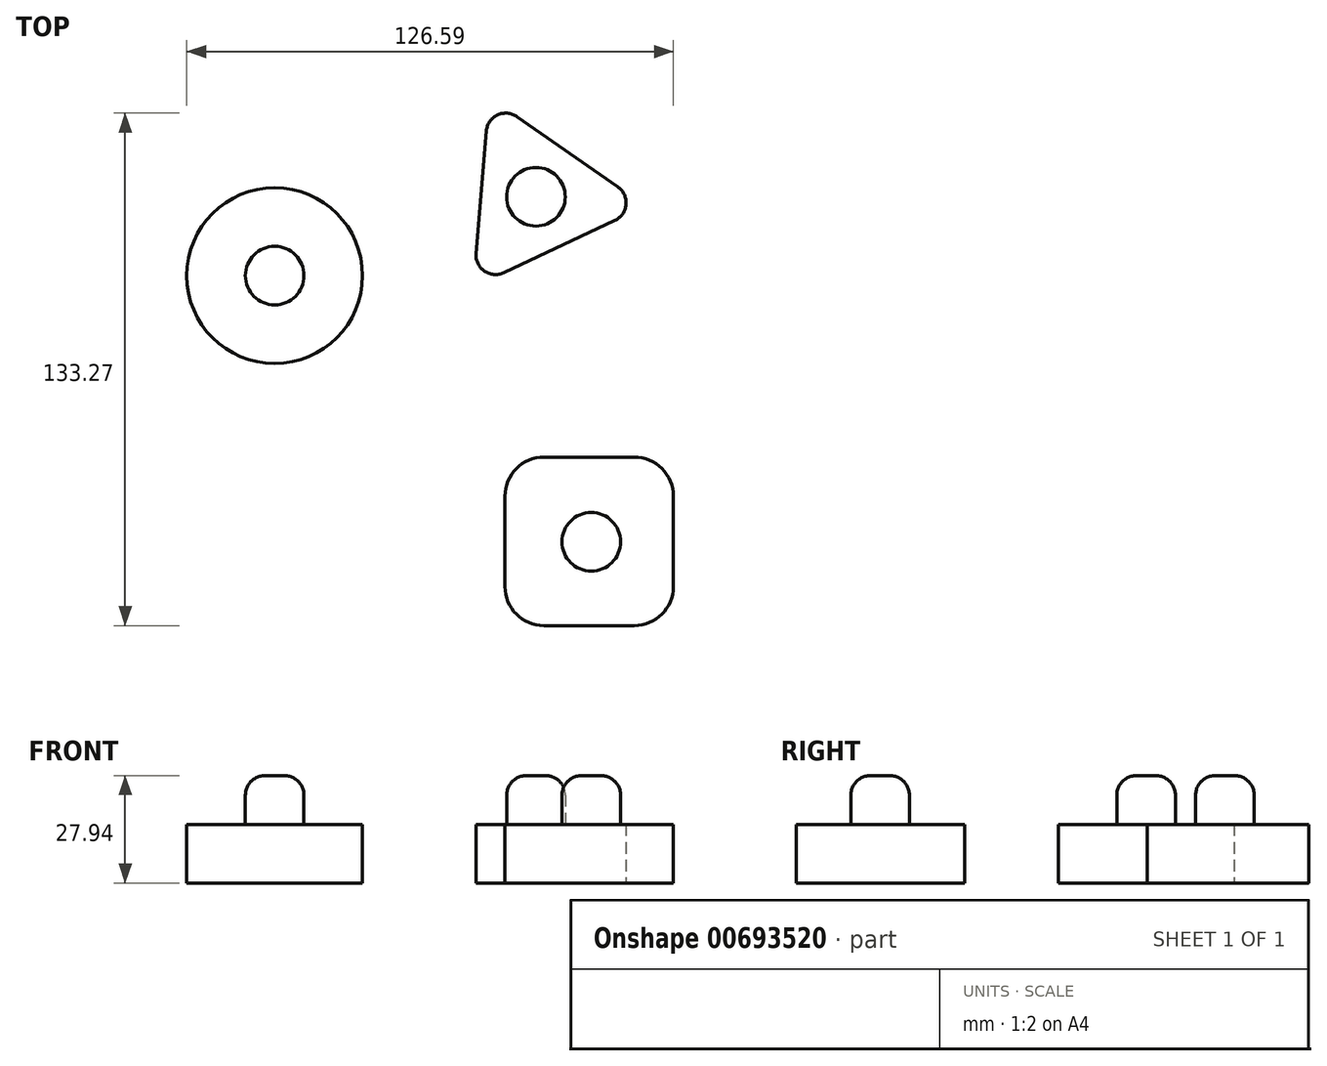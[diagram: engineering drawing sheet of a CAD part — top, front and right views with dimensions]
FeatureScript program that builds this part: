
annotation { "Feature Type Name" : "Feature", "Feature Type Description" : "" }
export const myFeature = defineFeature(function(context is Context, id is Id, definition is map)
    precondition{}
    {
        {
            var Q0;
            Q0=qCreatedBy(makeId("Top.planeOp"),FACE);
            var sketch = newSketch(context, id + "F0", { "sketchPlane" : qUnion([Q0])});
            skCircle(sketch, "E0", {"center": v(-45.19, 36.23) * mm, "radius": 22.86 * mm});
            skCircle(sketch, "E1", {"center": v(-45.19, 36.23) * mm, "radius": 7.62 * mm});
            skSolve(sketch);
        }
        {
            var Q0;
            Q0 = qSketchRegion(id + "F0", true);
            extrude(context, id + "F1", {"entities" : qUnion([Q0]), "depth" : 15.24 * mm, "offsetDistance" : 25.4 * mm});
        }
        {
            var Q0;
            Q0=qCreatedBy(makeId("Top.planeOp"),FACE);
            var sketch = newSketch(context, id + "F2", { "sketchPlane" : qUnion([Q0])});
            skLineSegment(sketch, "E2.bottom", {"start": v(24.88, -10.96) * mm, "end": v(48.38, -10.96) * mm});
            skLineSegment(sketch, "E2.top", {"start": v(24.88, -54.77) * mm, "end": v(48.38, -54.77) * mm});
            skLineSegment(sketch, "E2.left", {"start": v(14.72, -21.12) * mm, "end": v(14.72, -44.61) * mm});
            skLineSegment(sketch, "E2.right", {"start": v(58.54, -21.12) * mm, "end": v(58.54, -44.61) * mm});
            skPoint(sketch, "E3.visualSharp", {"position": v(14.72, -10.96) * mm});
            skArc(sketch, "E3.filletArc", {"start": v(24.88, -10.96) * mm, "mid": v(17.7, -13.93) * mm, "end": v(14.72, -21.12) * mm});
            skPoint(sketch, "E4.visualSharp", {"position": v(14.72, -54.77) * mm});
            skArc(sketch, "E4.filletArc", {"start": v(14.72, -44.61) * mm, "mid": v(17.7, -51.8) * mm, "end": v(24.88, -54.77) * mm});
            skPoint(sketch, "E5.visualSharp", {"position": v(58.54, -54.77) * mm});
            skArc(sketch, "E5.filletArc", {"start": v(48.38, -54.77) * mm, "mid": v(55.56, -51.8) * mm, "end": v(58.54, -44.61) * mm});
            skPoint(sketch, "E6.visualSharp", {"position": v(58.54, -10.96) * mm});
            skArc(sketch, "E7.filletArc", {"start": v(58.54, -21.12) * mm, "mid": v(55.56, -13.93) * mm, "end": v(48.38, -10.96) * mm});
            skCircle(sketch, "E8", {"center": v(37.19, -32.98) * mm, "radius": 7.62 * mm});
            skSolve(sketch);
        }
        {
            var Q0;
            Q0=makeQuery(id+"F2.imprint","IMPRINT",FACE,{"disambiguationData":[TD([[makeQuery(id+"F2.imprint","IMPRINT",EDGE,{"derivedFrom":sQuery(id+"F2.wireOp",EDGE,"E2.bottom")}),-1.0]])]});
            extrude(context, id + "F3", {"entities" : qUnion([Q0]), "depth" : 15.24 * mm, "offsetDistance" : 25.4 * mm});
        }
        {
            var Q0;
            Q0=qCreatedBy(makeId("Top.planeOp"),FACE);
            var sketch = newSketch(context, id + "F4", { "sketchPlane" : qUnion([Q0])});
            skCircle(sketch, "E9.cCircle", {"center": v(22.8, 56.73) * mm, "radius": 14.3 * mm, "construction": true});
            skLineSegment(sketch, "E9.0", {"start": v(43.33, 50.58) * mm, "end": v(14.43, 37) * mm});
            skLineSegment(sketch, "E9.1", {"start": v(7.2, 42.02) * mm, "end": v(9.9, 73.84) * mm});
            skLineSegment(sketch, "E9.2", {"start": v(17.86, 77.59) * mm, "end": v(44.07, 59.35) * mm});
            skPoint(sketch, "E9.0.midPoint", {"position": v(28.88, 43.8) * mm});
            skPoint(sketch, "E10.visualSharp", {"position": v(10.64, 82.61) * mm});
            skArc(sketch, "E10.filletArc", {"start": v(17.86, 77.59) * mm, "mid": v(12.8, 78.01) * mm, "end": v(9.9, 73.84) * mm});
            skPoint(sketch, "E11.visualSharp", {"position": v(51.3, 54.33) * mm});
            skArc(sketch, "E11.filletArc", {"start": v(43.33, 50.58) * mm, "mid": v(46.23, 54.75) * mm, "end": v(44.07, 59.35) * mm});
            skPoint(sketch, "E12.visualSharp", {"position": v(6.47, 33.26) * mm});
            skArc(sketch, "E12.filletArc", {"start": v(7.2, 42.02) * mm, "mid": v(9.37, 37.43) * mm, "end": v(14.43, 37) * mm});
            skCircle(sketch, "E13", {"center": v(22.8, 56.73) * mm, "radius": 7.62 * mm});
            skSolve(sketch);
        }
        {
            var Q0;
            Q0 = qSketchRegion(id + "F4", true);
            extrude(context, id + "F5", {"entities" : qUnion([Q0]), "depth" : 15.24 * mm, "offsetDistance" : 25.4 * mm});
        }
        {
            var Q0;
            Q0=makeQuery(id+"F2.imprint","IMPRINT",FACE,{"disambiguationData":[TD([[makeQuery(id+"F2.imprint","IMPRINT",EDGE,{"derivedFrom":sQuery(id+"F2.wireOp",EDGE,"E8")}),1.0]])]});
            extrude(context, id + "F6", {"entities" : qUnion([Q0]), "operationType" : NewBodyOperationType.ADD, "depth" : 27.94 * mm, "offsetDistance" : 25.4 * mm});
        }
        {
            var Q0;
            Q0=makeQuery(id+"F6.opExtrude","CAP_EDGE",EDGE,{"disambiguationData":[OSD([sQuery(id+"F2.wireOp",EDGE,"E8")])],"isStart":false});
            fillet(context, id + "F7", {"entities" : qUnion([Q0]), "radius" : 5.08 * mm, "tangentPropagation" : true, "allowEdgeOverflow" : false});
        }
        {
            var Q0;
            Q0=makeQuery(id+"F0.imprint","IMPRINT",FACE,{"disambiguationData":[TD([[makeQuery(id+"F0.imprint","IMPRINT",EDGE,{"derivedFrom":sQuery(id+"F0.wireOp",EDGE,"E1")}),1.0]])]});
            extrude(context, id + "F8", {"entities" : qUnion([Q0]), "operationType" : NewBodyOperationType.ADD, "depth" : 27.94 * mm, "offsetDistance" : 25.4 * mm});
        }
        {
            var Q0;
            Q0=makeQuery(id+"F8.opExtrude","CAP_EDGE",EDGE,{"disambiguationData":[OSD([sQuery(id+"F0.wireOp",EDGE,"E1")])],"isStart":false});
            fillet(context, id + "F9", {"entities" : qUnion([Q0]), "radius" : 5.08 * mm, "tangentPropagation" : true, "allowEdgeOverflow" : false});
        }
        {
            var Q0;
            Q0=makeQuery(id+"F4.imprint","IMPRINT",FACE,{"disambiguationData":[TD([[makeQuery(id+"F4.imprint","IMPRINT",EDGE,{"derivedFrom":sQuery(id+"F4.wireOp",EDGE,"E13")}),1.0]])]});
            extrude(context, id + "F10", {"entities" : qUnion([Q0]), "operationType" : NewBodyOperationType.ADD, "depth" : 27.94 * mm, "offsetDistance" : 25.4 * mm});
        }
        {
            var Q0;
            Q0=makeQuery(id+"F10.opExtrude","CAP_EDGE",EDGE,{"disambiguationData":[OSD([sQuery(id+"F4.wireOp",EDGE,"E13")])],"isStart":false});
            fillet(context, id + "F11", {"entities" : qUnion([Q0]), "radius" : 5.08 * mm, "tangentPropagation" : true, "allowEdgeOverflow" : false});
        }
    });
